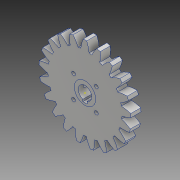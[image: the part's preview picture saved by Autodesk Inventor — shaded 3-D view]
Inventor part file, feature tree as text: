
AUTODESK INVENTOR PART (.ipt)
format: ipt  version: 2020 (Build 240168000, 168)  size: 318,976 bytes
history: native  units: mm
features: sketch x7, extrude x6, other x2
ambient origin geometry x8: Origin, YZ Plane, XZ Plane, XY Plane, X Axis, Y Axis, Z Axis, Center Point
bodies: Solid1 (feature_tree)
feature tree (15):
  extrude  "Extrusion1"  Depth=32.0mm
  extrude  "Extrusion2"  Depth=1e-05mm
  extrude  "Extrusion4"  Depth=15.0mm TaperAngle=0.0deg
  extrude  "Extrusion5"  Depth=10.0mm
  extrude  "Extrusion6"  Depth=5.2mm
  sketch  "Sketch8"  dims[d18=10.0mm d19=30.0mm d20=0.0mm]
  other  "Spur Gear Teeth7"
  extrude  "Extrusion7"  Depth=10.0mm TaperAngle=0.0deg
  sketch  "Sketch1"  dims[d0=20.0mm d1=32.0mm]
  sketch  "Sketch2"  dims[d2=1e-05mm d3=0.0mm d4=20.0mm]
  sketch  "Sketch4"  dims[d5=200.0mm d6=15.0mm d7=0.0mm]
  sketch  "Sketch5"  dims[d13=5.2mm d14=10.0mm]
  sketch  "Sketch6"  dims[d15=30.0mm d16=0.0mm d17=5.2mm]
  other  "Spur Gear1"
  sketch  "Sketch9"  dims[d21=6.1mm d22=3.0mm d23=0.0mm d24=0.0mm d25=50.0mm d26=25.0mm d27=25.0mm d28=5.55mm d29=8.0mm d30=8.0mm d31=8.0mm d32=8.0mm d33=8.0mm d34=8.0mm d35=8.0mm d36=8.0mm d37=0.0mm d38=0.0mm]
